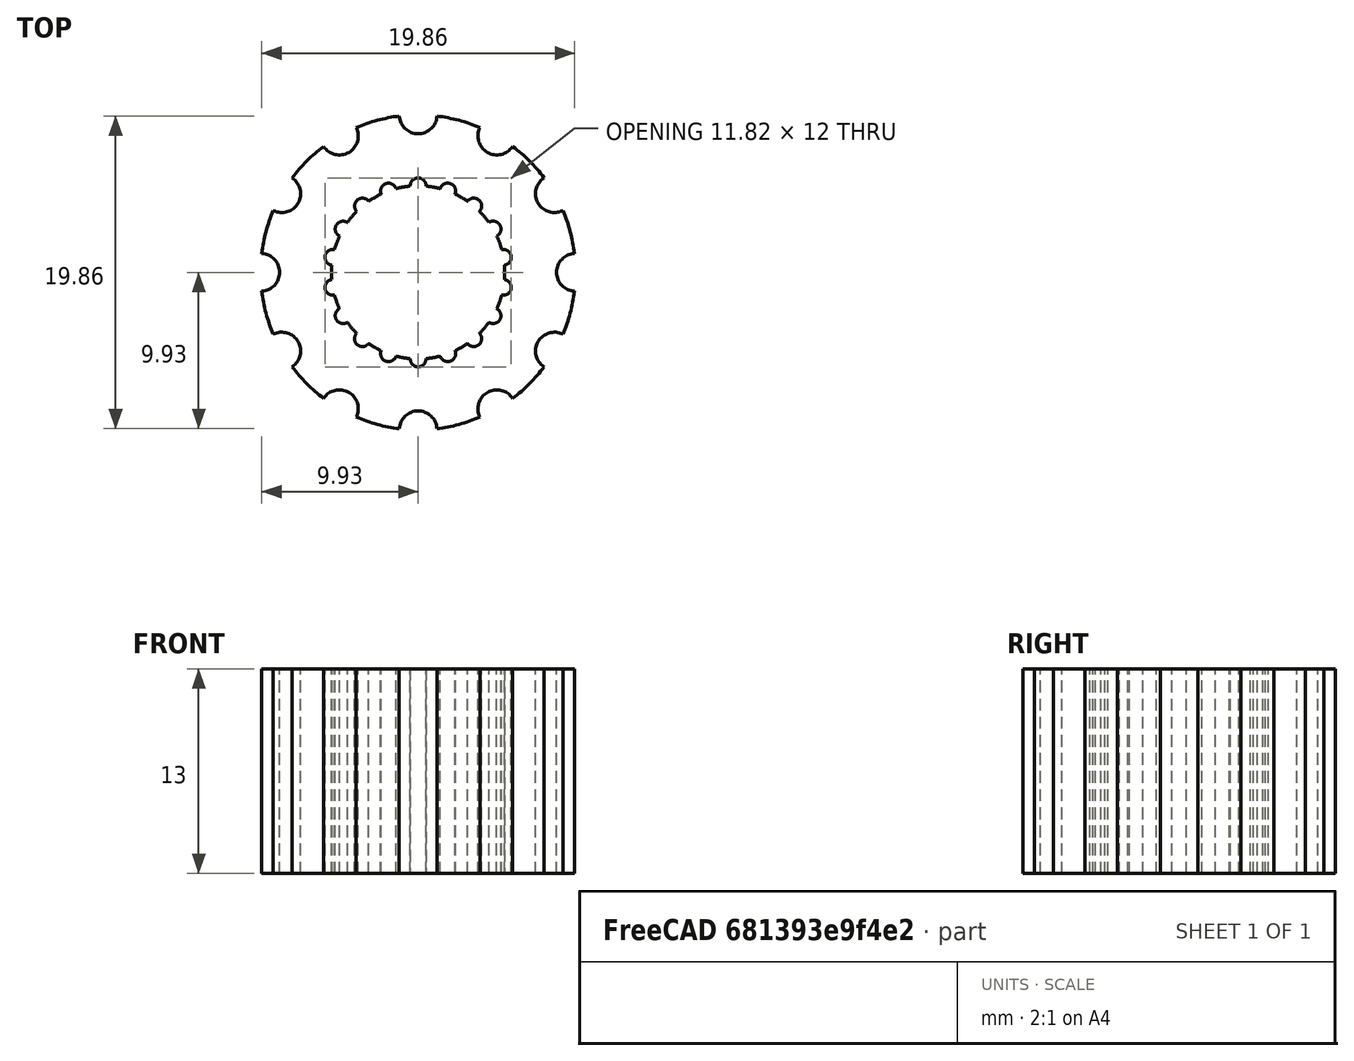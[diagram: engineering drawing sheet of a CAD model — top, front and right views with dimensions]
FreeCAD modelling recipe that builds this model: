
FCSTD DOCUMENT  (FreeCAD 0.19R)
Label: PumpValve
License: All rights reserved
LicenseURL: http://en.wikipedia.org/wiki/All_rights_reserved
objects: Sketcher::SketchObject×4, PartDesign::Pocket×3, PartDesign::PolarPattern×2, PartDesign::Pad×1, PartDesign::Body×1, Mesh::Feature×1
note: 15 computed .brp shape members not serialized (recipe doc carries the construction recipe); baked Part::Feature solids carry a one-line shape summary decoded from their .brp

FEATURE [Sketcher::SketchObject] Sketch
  FullyConstrained = true
  MapMode = 5
  Support = -> [XY_Plane]
  sketch-geometry (1):
    g0: Circle CenterX=0 CenterY=0 CenterZ=0 NormalX=0 NormalY=0 NormalZ=1 AngleXU=0 Radius=10
  constraints (2):
    c: Coincident(g0,g-1)
    c: Radius(g0) = 10
FEATURE [PartDesign::Pad] Pad
  Direction = (1,1,1)
  Length = 13
  Length2 = 100
  Profile = -> Sketch
  Type = 0
FEATURE [Sketcher::SketchObject] Sketch001
  FullyConstrained = true
  MapMode = 5
  Placement = pos=(0,0,13) rot=(0,0,1;0rad)
  Support = -> [Pad]
  sketch-geometry (1):
    g0: Circle CenterX=0 CenterY=0 CenterZ=0 NormalX=0 NormalY=0 NormalZ=1 AngleXU=0 Radius=5.5
  constraints (2):
    c: Radius(g0) = 5.5
    c: Coincident(g0,g-1)
FEATURE [PartDesign::Pocket] Pocket
  BaseFeature = -> Pad
  Length = 5
  Length2 = 100
  Profile = -> Sketch001
  Type = 1
FEATURE [Sketcher::SketchObject] Sketch002
  ExternalGeometry = -> [Pocket]
  FullyConstrained = true
  MapMode = 5
  Placement = pos=(0,0,13) rot=(0,0,1;0rad)
  Support = -> [Pocket]
  sketch-geometry (1):
    g0: Circle CenterX=0 CenterY=10 CenterZ=0 NormalX=0 NormalY=0 NormalZ=1 AngleXU=0 Radius=1.2
  constraints (3):
    c: Radius(g0) = 1.2
    c: PointOnObject(g0,g-2)
    c: PointOnObject(g0,g-3)
FEATURE [PartDesign::Pocket] Pocket001
  BaseFeature = -> Pocket
  Length = 5
  Length2 = 100
  Profile = -> Sketch002
  Type = 1
FEATURE [PartDesign::PolarPattern] PolarPattern
  Angle = 360
  Axis = -> Sketch002 [N_Axis]
  BaseFeature = -> Pocket001
  Occurrences = 12
  Originals = -> [Pocket001]
FEATURE [Sketcher::SketchObject] Sketch003
  ExternalGeometry = -> [PolarPattern]
  FullyConstrained = true
  MapMode = 5
  Placement = pos=(0,0,13) rot=(0,0,1;0rad)
  Support = -> [PolarPattern]
  sketch-geometry (1):
    g0: Circle CenterX=0 CenterY=5.5 CenterZ=0 NormalX=0 NormalY=0 NormalZ=1 AngleXU=0 Radius=0.5
  constraints (3):
    c: PointOnObject(g0,g-2)
    c: Radius(g0) = 0.5
    c: PointOnObject(g0,g-3)
FEATURE [PartDesign::Pocket] Pocket002
  BaseFeature = -> PolarPattern
  Length = 5
  Length2 = 100
  Profile = -> Sketch003
  Type = 1
FEATURE [PartDesign::PolarPattern] PolarPattern001
  Angle = 360
  Axis = -> Sketch003 [N_Axis]
  BaseFeature = -> Pocket002
  Occurrences = 18
  Originals = -> [Pocket002]
FEATURE [PartDesign::Body] Body
  Group = -> [Sketch,Pad,Sketch001,Pocket,Sketch002,Pocket001,PolarPattern,Sketch003,Pocket002,PolarPattern001]
  Origin = -> Origin
  Tip = -> PolarPattern001
FEATURE [Mesh::Feature] Mesh  label="PolarPattern001 (Meshed)"
